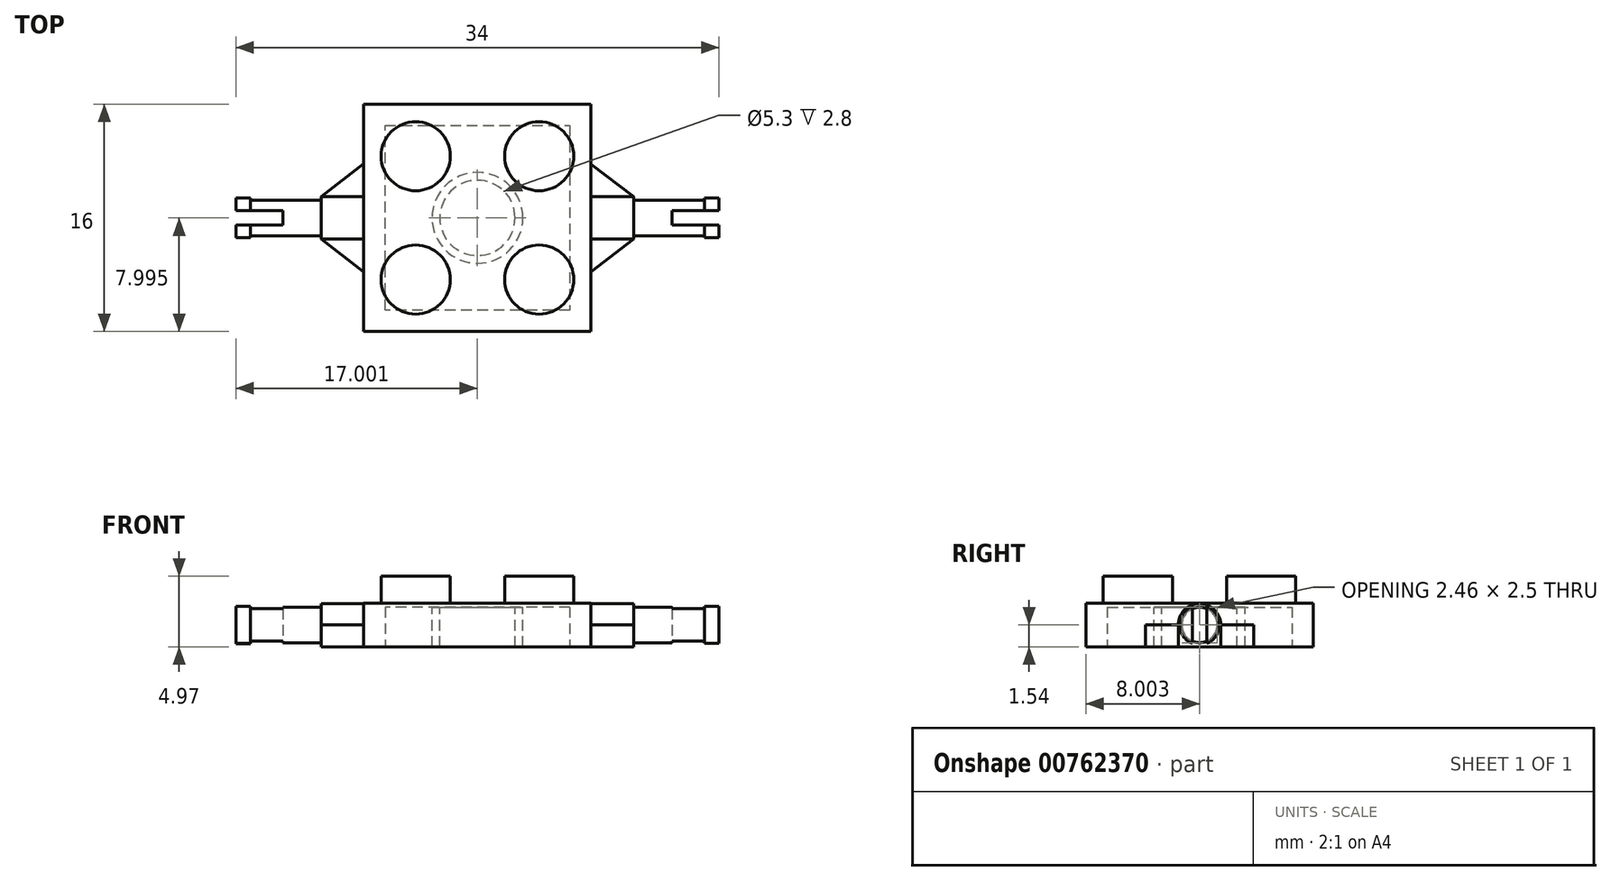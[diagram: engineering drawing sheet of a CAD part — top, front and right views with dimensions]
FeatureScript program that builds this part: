
annotation { "Feature Type Name" : "Feature", "Feature Type Description" : "" }
export const myFeature = defineFeature(function(context is Context, id is Id, definition is map)
    precondition{}
    {
        {
            var Q0;
            Q0=qCreatedBy(makeId("Top.planeOp"),FACE);
            var sketch = newSketch(context, id + "F0", { "sketchPlane" : qUnion([Q0])});
            skLineSegment(sketch, "E0", {"start": v(-18.34, 23.52) * mm, "end": v(-2.34, 23.52) * mm});
            skLineSegment(sketch, "E1", {"start": v(-18.34, 23.52) * mm, "end": v(-18.34, 7.52) * mm});
            skLineSegment(sketch, "E2", {"start": v(-18.34, 7.52) * mm, "end": v(-2.34, 7.52) * mm});
            skLineSegment(sketch, "E3", {"start": v(-2.34, 23.52) * mm, "end": v(-2.34, 7.52) * mm});
            skSolve(sketch);
        }
        {
            var Q0;
            Q0=qSketchRegion(id+"F0",true);
            extrude(context, id + "F1", {"entities" : qUnion([Q0]), "depth" : 3.08 * mm, "offsetDistance" : 25 * mm});
        }
        {
            var Q0;
            Q0=makeQuery(id+"F1.opExtrude","CAP_FACE",FACE,{"disambiguationData":[OSD([sQuery(id+"F0.wireOp",EDGE,"E0"),sQuery(id+"F0.wireOp",EDGE,"E1"),sQuery(id+"F0.wireOp",EDGE,"E2"),sQuery(id+"F0.wireOp",EDGE,"E3")])],"isStart":false});
            var sketch = newSketch(context, id + "F2", { "sketchPlane" : qUnion([Q0])});
            skCircle(sketch, "E4", {"center": v(-14.68, 19.86) * mm, "radius": 2.44 * mm});
            skCircle(sketch, "E5", {"center": v(-6, 19.86) * mm, "radius": 2.44 * mm});
            skCircle(sketch, "E6", {"center": v(-14.68, 11.17) * mm, "radius": 2.44 * mm});
            skCircle(sketch, "E7", {"center": v(-6, 11.17) * mm, "radius": 2.44 * mm});
            skSolve(sketch);
        }
        {
            var Q0;
            Q0=qSketchRegion(id+"F2",true);
            extrude(context, id + "F3", {"entities" : qUnion([Q0]), "operationType" : NewBodyOperationType.ADD, "depth" : 1.89 * mm, "offsetDistance" : 25 * mm});
        }
        {
            var Q0;
            Q0=makeQuery(id+"F1.opExtrude","SWEPT_FACE",FACE,{"disambiguationData":[OSD([sQuery(id+"F0.wireOp",EDGE,"E3")])]});
            var sketch = newSketch(context, id + "F4", { "sketchPlane" : qUnion([Q0])});
            skCircle(sketch, "E8", {"center": v(15.52, 1.54) * mm, "radius": 1.5 * mm});
            skPoint(sketch, "E8.centerSnap0", {"position": v(23.52, 1.54) * mm});
            skPoint(sketch, "E8.centerSnap1", {"position": v(15.52, 3.08) * mm});
            skSolve(sketch);
        }
        {
            var Q0;
            Q0=qSketchRegion(id+"F4",true);
            extrude(context, id + "F5", {"entities" : qUnion([Q0]), "operationType" : NewBodyOperationType.ADD, "depth" : 3 * mm, "offsetDistance" : 25 * mm});
        }
        {
            var Q0;
            Q0=makeQuery(id+"F1.opExtrude","SWEPT_FACE",FACE,{"disambiguationData":[OSD([sQuery(id+"F0.wireOp",EDGE,"E1")])]});
            var sketch = newSketch(context, id + "F6", { "sketchPlane" : qUnion([Q0])});
            skCircle(sketch, "E9", {"center": v(-15.52, 1.54) * mm, "radius": 1.5 * mm});
            skPoint(sketch, "E9.centerSnap0", {"position": v(-7.52, 1.54) * mm});
            skPoint(sketch, "E9.centerSnap1", {"position": v(-15.52, 3.08) * mm});
            skSolve(sketch);
        }
        {
            var Q0;
            Q0=qSketchRegion(id+"F6",true);
            extrude(context, id + "F7", {"entities" : qUnion([Q0]), "operationType" : NewBodyOperationType.ADD, "depth" : 3 * mm, "offsetDistance" : 25 * mm});
        }
        {
            var Q0;
            Q0=makeQuery(id+"F7.opExtrude","CAP_FACE",FACE,{"disambiguationData":[OSD([sQuery(id+"F6.wireOp",EDGE,"E9")])],"isStart":false});
            var sketch = newSketch(context, id + "F8", { "sketchPlane" : qUnion([Q0])});
            skCircle(sketch, "E10", {"center": v(-15.52, 1.54) * mm, "radius": 1.25 * mm});
            skSolve(sketch);
        }
        {
            var Q0;
            Q0=qSketchRegion(id+"F8",true);
            extrude(context, id + "F9", {"entities" : qUnion([Q0]), "operationType" : NewBodyOperationType.ADD, "depth" : 5 * mm, "offsetDistance" : 25 * mm});
        }
        {
            var Q0;
            Q0=makeQuery(id+"F5.opExtrude","CAP_FACE",FACE,{"disambiguationData":[OSD([sQuery(id+"F4.wireOp",EDGE,"E8")])],"isStart":false});
            var sketch = newSketch(context, id + "F10", { "sketchPlane" : qUnion([Q0])});
            skCircle(sketch, "E11", {"center": v(15.52, 1.54) * mm, "radius": 1.25 * mm});
            skSolve(sketch);
        }
        {
            var Q0;
            Q0=qSketchRegion(id+"F10",true);
            extrude(context, id + "F11", {"entities" : qUnion([Q0]), "operationType" : NewBodyOperationType.ADD, "depth" : 5 * mm, "offsetDistance" : 25 * mm});
        }
        {
            var Q0;
            Q0=makeQuery(id+"F1.opExtrude","SWEPT_FACE",FACE,{"disambiguationData":[OSD([sQuery(id+"F0.wireOp",EDGE,"E1")])]});
            var sketch = newSketch(context, id + "F12", { "sketchPlane" : qUnion([Q0])});
            skLineSegment(sketch, "E12", {"start": v(-19.32, 1.54) * mm, "end": v(-19.32, 0) * mm});
            skPoint(sketch, "E12.startSnap0", {"position": v(-23.52, 1.54) * mm});
            skLineSegment(sketch, "E13", {"start": v(-19.32, 0) * mm, "end": v(-11.72, 0) * mm});
            skLineSegment(sketch, "E14", {"start": v(-11.72, 0) * mm, "end": v(-11.72, 1.54) * mm});
            skLineSegment(sketch, "E15", {"start": v(-11.72, 1.54) * mm, "end": v(-14.02, 1.54) * mm});
            skLineSegment(sketch, "E16", {"start": v(-19.32, 1.54) * mm, "end": v(-17.02, 1.54) * mm});
            skSolve(sketch);
        }
        {
            var Q0;
            Q0=qSketchRegion(id+"F12",true);
            var Q1;
            Q1=makeQuery(id+"F12.imprint","IMPRINT",FACE,{"disambiguationData":[TD([[makeQuery(id+"F12.imprint","IMPRINT",EDGE,{"derivedFrom":sQuery(id+"F12.wireOp",EDGE,"E12")}),1.0]])]});
            extrude(context, id + "F13", {"entities" : qUnion([Q0, Q1]), "operationType" : NewBodyOperationType.ADD, "depth" : 3 * mm, "offsetDistance" : 25 * mm});
        }
        {
            var Q0;
            Q0=makeQuery(id+"F1.opExtrude","SWEPT_FACE",FACE,{"disambiguationData":[OSD([sQuery(id+"F0.wireOp",EDGE,"E3")])]});
            var sketch = newSketch(context, id + "F14", { "sketchPlane" : qUnion([Q0])});
            skLineSegment(sketch, "E17", {"start": v(11.72, 1.54) * mm, "end": v(11.72, 0) * mm});
            skPoint(sketch, "E17.startSnap0", {"position": v(7.52, 1.54) * mm});
            skLineSegment(sketch, "E18", {"start": v(11.72, 0) * mm, "end": v(19.32, 0) * mm});
            skLineSegment(sketch, "E19", {"start": v(19.32, 0) * mm, "end": v(19.32, 1.54) * mm});
            skLineSegment(sketch, "E20", {"start": v(19.32, 1.54) * mm, "end": v(17.02, 1.54) * mm});
            skLineSegment(sketch, "E21", {"start": v(11.72, 1.54) * mm, "end": v(14.02, 1.54) * mm});
            skSolve(sketch);
        }
        {
            var Q0;
            Q0=qSketchRegion(id+"F14",true);
            var Q1;
            Q1=makeQuery(id+"F14.imprint","IMPRINT",FACE,{"disambiguationData":[TD([[makeQuery(id+"F14.imprint","IMPRINT",EDGE,{"derivedFrom":sQuery(id+"F14.wireOp",EDGE,"E17")}),1.0]])]});
            extrude(context, id + "F15", {"entities" : qUnion([Q0, Q1]), "operationType" : NewBodyOperationType.ADD, "depth" : 3 * mm, "offsetDistance" : 25 * mm});
        }
        {
            var Q0;
            Q0=makeQuery(id+"F13.opExtrude","SWEPT_FACE",FACE,{"disambiguationData":[OSD([sQuery(id+"F12.wireOp",EDGE,"E16")])]});
            var sketch = newSketch(context, id + "F16", { "sketchPlane" : qUnion([Q0])});
            skLineSegment(sketch, "E22", {"start": v(-18.34, 19.32) * mm, "end": v(-21.34, 19.32) * mm});
            skLineSegment(sketch, "E23", {"start": v(-21.34, 19.32) * mm, "end": v(-21.34, 17.02) * mm});
            skLineSegment(sketch, "E24", {"start": v(-21.34, 17.02) * mm, "end": v(-18.34, 19.32) * mm});
            skLineSegment(sketch, "E25", {"start": v(-21.34, 11.72) * mm, "end": v(-21.34, 14.02) * mm});
            skLineSegment(sketch, "E26", {"start": v(-21.34, 14.02) * mm, "end": v(-18.34, 11.72) * mm});
            skLineSegment(sketch, "E27", {"start": v(-18.34, 11.72) * mm, "end": v(-21.34, 11.72) * mm});
            skSolve(sketch);
        }
        {
            var Q0;
            Q0=makeQuery(id+"F16.imprint","IMPRINT",FACE,{"disambiguationData":[TD([[makeQuery(id+"F16.imprint","IMPRINT",EDGE,{"derivedFrom":sQuery(id+"F16.wireOp",EDGE,"E25")}),-1.0]])]});
            var Q1;
            Q1=makeQuery(id+"F16.imprint","IMPRINT",FACE,{"disambiguationData":[TD([[makeQuery(id+"F16.imprint","IMPRINT",EDGE,{"derivedFrom":sQuery(id+"F16.wireOp",EDGE,"E22")}),-1.0]])]});
            extrude(context, id + "F17", {"entities" : qUnion([Q0, Q1]), "operationType" : NewBodyOperationType.REMOVE, "oppositeDirection" : true, "depth" : 25 * mm, "offsetDistance" : 25 * mm});
        }
        {
            var Q0;
            Q0=makeQuery(id+"F15.opExtrude","SWEPT_FACE",FACE,{"disambiguationData":[OSD([sQuery(id+"F14.wireOp",EDGE,"E21")])]});
            var sketch = newSketch(context, id + "F18", { "sketchPlane" : qUnion([Q0])});
            skLineSegment(sketch, "E28", {"start": v(-2.34, 11.72) * mm, "end": v(0.66, 11.72) * mm});
            skLineSegment(sketch, "E29", {"start": v(0.66, 11.72) * mm, "end": v(0.66, 14.02) * mm});
            skLineSegment(sketch, "E30", {"start": v(0.66, 14.02) * mm, "end": v(-2.34, 11.72) * mm});
            skLineSegment(sketch, "E31", {"start": v(-2.34, 19.31) * mm, "end": v(0.66, 17.01) * mm});
            skPoint(sketch, "E32.start.orphan", {"position": v(-2.34, 17.01) * mm});
            skLineSegment(sketch, "E33", {"start": v(-2.34, 19.31) * mm, "end": v(0.66, 19.31) * mm});
            skLineSegment(sketch, "E34", {"start": v(0.66, 19.31) * mm, "end": v(0.66, 17.01) * mm});
            skSolve(sketch);
        }
        {
            var Q0;
            Q0=qSketchRegion(id+"F18",true);
            extrude(context, id + "F19", {"entities" : qUnion([Q0]), "operationType" : NewBodyOperationType.REMOVE, "oppositeDirection" : true, "depth" : 25 * mm, "offsetDistance" : 25 * mm});
        }
        {
            var Q0;
            Q0=makeQuery(id+"F9.opExtrude","CAP_FACE",FACE,{"disambiguationData":[OSD([sQuery(id+"F8.wireOp",EDGE,"E10")])],"isStart":false});
            var sketch = newSketch(context, id + "F20", { "sketchPlane" : qUnion([Q0])});
            skLineSegment(sketch, "E35", {"start": v(-16.02, 2.69) * mm, "end": v(-16.02, 0.4) * mm});
            skLineSegment(sketch, "E36", {"start": v(-15.02, 2.69) * mm, "end": v(-15.02, 0.4) * mm});
            skSolve(sketch);
        }
        {
            var Q0;
            Q0=qSketchRegion(id+"F20",true);
            var Q1;
            {var subQ0=sQuery(id+"F20.wireOp",EDGE,"E35");Q1=makeQuery(id+"F20.imprint","IMPRINT",FACE,{"disambiguationData":[TD([[makeQuery(id+"F20.imprint","IMPRINT",EDGE,{"derivedFrom":subQ0}),1.0]])]});}
            extrude(context, id + "F21", {"entities" : qUnion([Q0, Q1]), "operationType" : NewBodyOperationType.REMOVE, "oppositeDirection" : true, "depth" : 2.3 * mm, "offsetDistance" : 25 * mm});
        }
        {
            var Q0;
            Q0=makeQuery(id+"F11.opExtrude","CAP_FACE",FACE,{"disambiguationData":[OSD([sQuery(id+"F10.wireOp",EDGE,"E11")])],"isStart":false});
            var sketch = newSketch(context, id + "F22", { "sketchPlane" : qUnion([Q0])});
            skLineSegment(sketch, "E37", {"start": v(15.02, 2.69) * mm, "end": v(15.02, 0.4) * mm});
            skLineSegment(sketch, "E38", {"start": v(16.02, 2.69) * mm, "end": v(16.02, 0.4) * mm});
            skSolve(sketch);
        }
        {
            var Q0;
            Q0=qSketchRegion(id+"F22",true);
            var Q1;
            {var subQ0=sQuery(id+"F22.wireOp",EDGE,"E37");Q1=makeQuery(id+"F22.imprint","IMPRINT",FACE,{"disambiguationData":[TD([[makeQuery(id+"F22.imprint","IMPRINT",EDGE,{"derivedFrom":subQ0}),1.0]])]});}
            extrude(context, id + "F23", {"entities" : qUnion([Q0, Q1]), "operationType" : NewBodyOperationType.REMOVE, "oppositeDirection" : true, "depth" : 2.3 * mm, "offsetDistance" : 25 * mm});
        }
        {
            var Q0;
            {var subQ0=sQuery(id+"F8.wireOp",EDGE,"E10");Q0=makeQuery(id+"F21.boolean.opBoolean","SPLIT",FACE,{"disambiguationData":[TD([makeQuery(id+"F21.opExtrude","SWEPT_FACE",FACE,{"disambiguationData":[OSD([sQuery(id+"F20.wireOp",EDGE,"E36")])]})])],"derivedFrom":makeQuery(id+"F9.opExtrude","CAP_FACE",FACE,{"disambiguationData":[OSD([subQ0])],"isStart":false})});}
            var sketch = newSketch(context, id + "F24", { "sketchPlane" : qUnion([Q0])});
            skCircle(sketch, "E39", {"center": v(-15.52, 1.54) * mm, "radius": 1.4 * mm});
            skLineSegment(sketch, "E40", {"start": v(-16.02, 2.85) * mm, "end": v(-16.02, 0.23) * mm});
            skLineSegment(sketch, "E41", {"start": v(-15.02, 2.85) * mm, "end": v(-15.02, 0.23) * mm});
            skSolve(sketch);
        }
        {
            var Q0;
            {var subQ4=sQuery(id+"F8.wireOp",EDGE,"E10");var subQ5=makeQuery(id+"F21.boolean.opBoolean","SPLIT",EDGE,{"disambiguationData":[TD([makeQuery(id+"F21.opExtrude","SWEPT_FACE",FACE,{"disambiguationData":[OSD([sQuery(id+"F20.wireOp",EDGE,"E36")])]})])],"derivedFrom":makeQuery(id+"F9.opExtrude","CAP_EDGE",EDGE,{"disambiguationData":[OSD([subQ4])],"isStart":false})});Q0=makeQuery(id+"F24.imprint","IMPRINT",FACE,{"disambiguationData":[TD([[makeQuery(id+"F24.imprint","IMPRINT",EDGE,{"derivedFrom":subQ5}),-1.0]])]});}
            var Q1;
            {var subQ0=sQuery(id+"F24.wireOp",EDGE,"E40");Q1=makeQuery(id+"F24.imprint","IMPRINT",FACE,{"disambiguationData":[TD([[makeQuery(id+"F24.imprint","IMPRINT",EDGE,{"derivedFrom":subQ0}),-1.0]])]});}
            var Q2;
            {var subQ1=sQuery(id+"F8.wireOp",EDGE,"E10");var subQ2=makeQuery(id+"F21.boolean.opBoolean","SPLIT",EDGE,{"disambiguationData":[TD([makeQuery(id+"F21.opExtrude","SWEPT_FACE",FACE,{"disambiguationData":[OSD([sQuery(id+"F20.wireOp",EDGE,"E36")])]})])],"derivedFrom":makeQuery(id+"F9.opExtrude","CAP_EDGE",EDGE,{"disambiguationData":[OSD([subQ1])],"isStart":false})});Q2=makeQuery(id+"F24.imprint","IMPRINT",FACE,{"disambiguationData":[TD([[makeQuery(id+"F24.imprint","IMPRINT",EDGE,{"derivedFrom":subQ2}),1.0]])]});}
            extrude(context, id + "F25", {"entities" : qUnion([Q0, Q1, Q2]), "operationType" : NewBodyOperationType.ADD, "depth" : 1 * mm, "offsetDistance" : 25 * mm});
        }
        {
            var Q0;
            {var subQ0=sQuery(id+"F10.wireOp",EDGE,"E11");Q0=makeQuery(id+"F23.boolean.opBoolean","SPLIT",FACE,{"disambiguationData":[TD([makeQuery(id+"F23.opExtrude","SWEPT_FACE",FACE,{"disambiguationData":[OSD([sQuery(id+"F22.wireOp",EDGE,"E37")])]})])],"derivedFrom":makeQuery(id+"F11.opExtrude","CAP_FACE",FACE,{"disambiguationData":[OSD([subQ0])],"isStart":false})});}
            var sketch = newSketch(context, id + "F26", { "sketchPlane" : qUnion([Q0])});
            skArc(sketch, "E42", {"start": v(15.02, 2.85) * mm, "mid": v(14.12, 1.54) * mm, "end": v(15.02, 0.23) * mm});
            skLineSegment(sketch, "E43", {"start": v(15.02, 2.85) * mm, "end": v(15.02, 0.23) * mm});
            skLineSegment(sketch, "E44", {"start": v(16.02, 2.85) * mm, "end": v(16.02, 0.23) * mm});
            skArc(sketch, "E45.trimOffspring", {"start": v(16.02, 0.23) * mm, "mid": v(16.92, 1.54) * mm, "end": v(16.02, 2.85) * mm});
            skSolve(sketch);
        }
        {
            var Q0;
            Q0=qSketchRegion(id+"F26",true);
            var Q1;
            Q1=qSketchRegion(id+"F28",true);
            extrude(context, id + "F27", {"entities" : qUnion([Q0, Q1]), "operationType" : NewBodyOperationType.ADD, "depth" : 1 * mm, "offsetDistance" : 25 * mm});
        }
        {
            var Q0;
            Q0=makeQuery(id+"F15.boolean.opBoolean","MERGE",FACE,{"derivedFrom":[makeQuery(id+"F13.boolean.opBoolean","MERGE",FACE,{"derivedFrom":[makeQuery(id+"F1.opExtrude","CAP_FACE",FACE,{"disambiguationData":[OSD([sQuery(id+"F0.wireOp",EDGE,"E0"),sQuery(id+"F0.wireOp",EDGE,"E1"),sQuery(id+"F0.wireOp",EDGE,"E2"),sQuery(id+"F0.wireOp",EDGE,"E3")])],"isStart":true}),makeQuery(id+"F13.opExtrude","SWEPT_FACE",FACE,{"disambiguationData":[OSD([sQuery(id+"F12.wireOp",EDGE,"E13")])]})]}),makeQuery(id+"F15.opExtrude","SWEPT_FACE",FACE,{"disambiguationData":[OSD([sQuery(id+"F14.wireOp",EDGE,"E18")])]})]});
            var sketch = newSketch(context, id + "F28", { "sketchPlane" : qUnion([Q0])});
            skLineSegment(sketch, "E46", {"start": v(-16.84, -9.02) * mm, "end": v(-16.84, -22.02) * mm});
            skLineSegment(sketch, "E47", {"start": v(-16.84, -22.02) * mm, "end": v(-3.84, -22.02) * mm});
            skLineSegment(sketch, "E48", {"start": v(-3.84, -22.02) * mm, "end": v(-3.84, -9.02) * mm});
            skLineSegment(sketch, "E49", {"start": v(-3.84, -9.02) * mm, "end": v(-16.84, -9.02) * mm});
            skSolve(sketch);
        }
        {
            var Q0;
            Q0=qSketchRegion(id+"F28",true);
            extrude(context, id + "F29", {"entities" : qUnion([Q0]), "operationType" : NewBodyOperationType.REMOVE, "oppositeDirection" : true, "depth" : 2.8 * mm, "offsetDistance" : 25 * mm});
        }
        {
            var Q0;
            Q0=makeQuery(id+"F29.boolean.opBoolean","COPY",FACE,{"derivedFrom":makeQuery(id+"F29.opExtrude","CAP_FACE",FACE,{"disambiguationData":[OSD([sQuery(id+"F28.wireOp",EDGE,"E46"),sQuery(id+"F28.wireOp",EDGE,"E47"),sQuery(id+"F28.wireOp",EDGE,"E48"),sQuery(id+"F28.wireOp",EDGE,"E49")])],"isStart":false})});
            var sketch = newSketch(context, id + "F30", { "sketchPlane" : qUnion([Q0])});
            skCircle(sketch, "E50", {"center": v(-10.34, -15.52) * mm, "radius": 3.2 * mm});
            skPoint(sketch, "E51.start.orphan", {"position": v(-16.84, -15.52) * mm});
            skPoint(sketch, "E52.trimOffspring.end.orphan", {"position": v(-3.84, -15.52) * mm});
            skCircle(sketch, "E53", {"center": v(-10.34, -15.52) * mm, "radius": 2.65 * mm});
            skSolve(sketch);
        }
        {
            var Q0;
            Q0=qSketchRegion(id+"F30",true);
            extrude(context, id + "F31", {"entities" : qUnion([Q0]), "operationType" : NewBodyOperationType.ADD, "depth" : 2.8 * mm, "offsetDistance" : 25 * mm});
        }
    });
